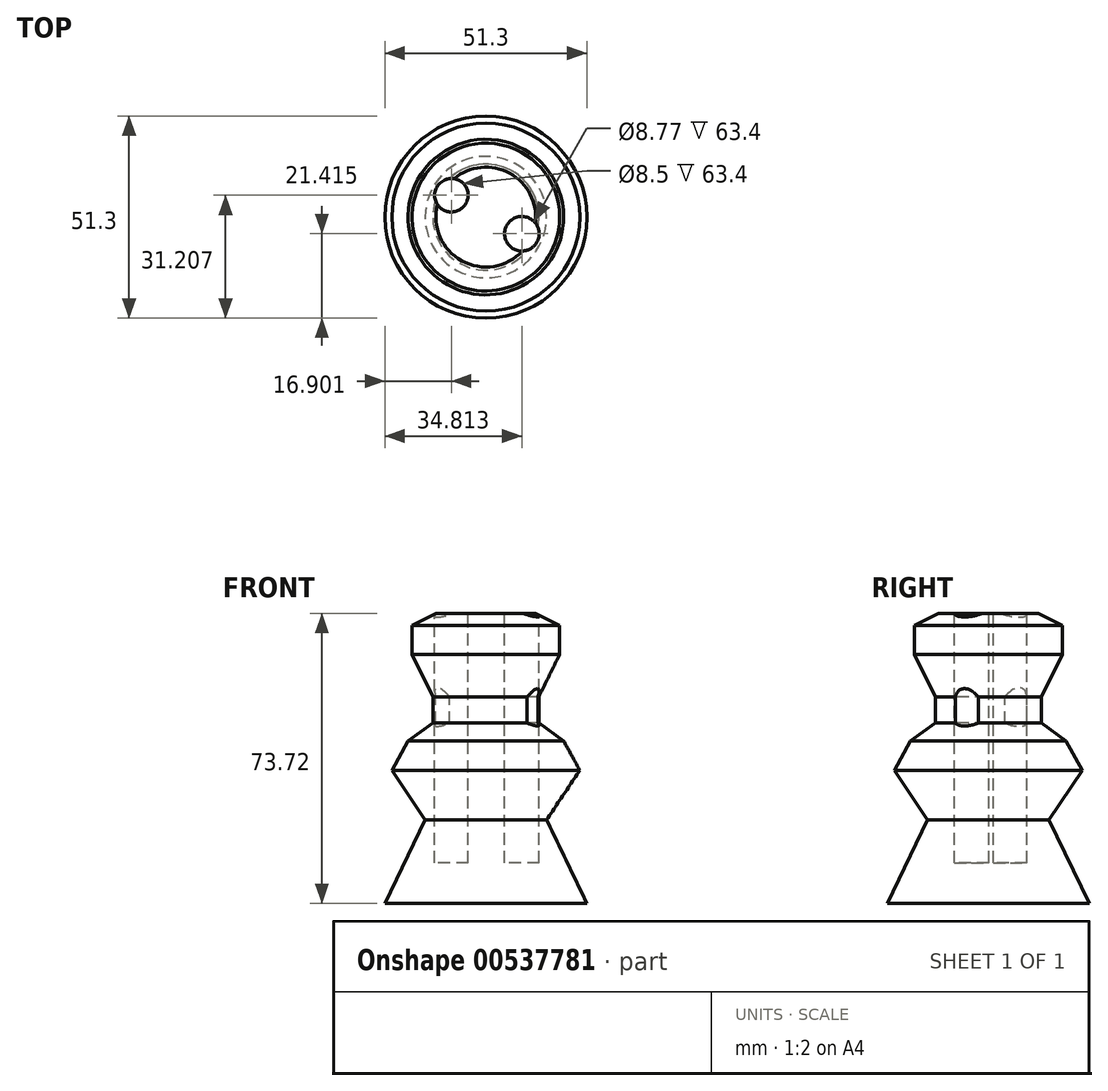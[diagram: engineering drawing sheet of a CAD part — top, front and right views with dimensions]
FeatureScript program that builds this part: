
annotation { "Feature Type Name" : "Feature", "Feature Type Description" : "" }
export const myFeature = defineFeature(function(context is Context, id is Id, definition is map)
    precondition{}
    {
        {
            var Q0;
            Q0=qCreatedBy(makeId("Front.planeOp"),FACE);
            var sketch = newSketch(context, id + "F0", { "sketchPlane" : qUnion([Q0])});
            skLineSegment(sketch, "E0", {"start": v(0, 51.3) * mm, "end": v(0, -47.77) * mm});
            skLineSegment(sketch, "E1", {"start": v(0, -26.74) * mm, "end": v(-25.65, -26.74) * mm});
            skLineSegment(sketch, "E2", {"start": v(-25.65, -26.74) * mm, "end": v(-15.43, -5.5) * mm});
            skLineSegment(sketch, "E3", {"start": v(-15.43, -5.5) * mm, "end": v(-23.89, 7.08) * mm});
            skLineSegment(sketch, "E4", {"start": v(-23.89, 7.08) * mm, "end": v(-19.76, 14.55) * mm});
            skLineSegment(sketch, "E5", {"start": v(-19.76, 14.55) * mm, "end": v(-13.47, 19.07) * mm});
            skLineSegment(sketch, "E6", {"start": v(-13.47, 19.07) * mm, "end": v(-13.47, 25.75) * mm});
            skLineSegment(sketch, "E7", {"start": v(-13.47, 25.75) * mm, "end": v(-18.77, 36.56) * mm});
            skLineSegment(sketch, "E8", {"start": v(-18.77, 36.56) * mm, "end": v(-18.77, 43.84) * mm});
            skLineSegment(sketch, "E9", {"start": v(-18.77, 43.84) * mm, "end": v(-12.68, 46.98) * mm});
            skLineSegment(sketch, "E10", {"start": v(-12.68, 46.98) * mm, "end": v(0, 46.98) * mm});
            skSolve(sketch);
        }
        {
            var Q0;
            Q0 = qSketchRegion(id + "F0", true);
            var Q1;
            Q1=sQuery(id+"F0.wireOp",EDGE,"E0");
            revolve(context, id + "F1", {"entities" : qUnion([Q0]), "axis" : qUnion([Q1]), "revolveType" : RevolveType.FULL});
        }
        {
            var Q0;
            Q0=makeQuery(id+"F1.opRevolve","SWEPT_FACE",FACE,{"disambiguationData":[OSD([sQuery(id+"F0.wireOp",EDGE,"E10")])]});
            var sketch = newSketch(context, id + "F2", { "sketchPlane" : qUnion([Q0])});
            skCircle(sketch, "E11", {"center": v(-8.75, 5.56) * mm, "radius": 4.25 * mm});
            skCircle(sketch, "E12", {"center": v(9.16, -4.24) * mm, "radius": 4.39 * mm});
            skSolve(sketch);
        }
        {
            var Q0;
            Q0 = qSketchRegion(id + "F2", true);
            extrude(context, id + "F3", {"entities" : qUnion([Q0]), "operationType" : NewBodyOperationType.REMOVE, "oppositeDirection" : true, "depth" : 63.4 * mm, "offsetDistance" : 25 * mm});
        }
    });
